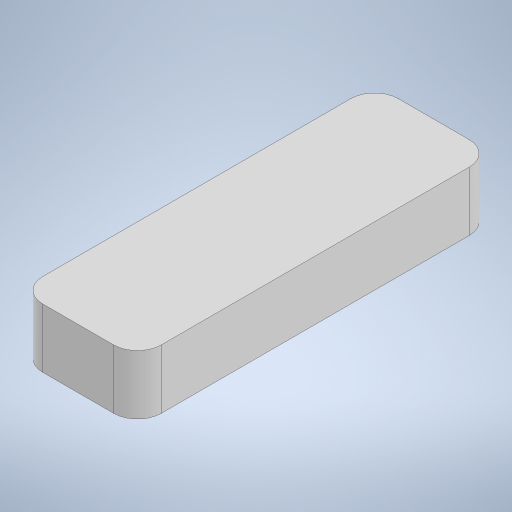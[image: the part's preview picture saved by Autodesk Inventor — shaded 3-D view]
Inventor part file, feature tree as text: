
AUTODESK INVENTOR PART (.ipt)
format: ipt  version: 2023 (Build 270158000, 158)  size: 203,264 bytes
history: native  units: mm
features: other x1, extrude x1, fillet x1, sketch x1
ambient origin geometry x8: Origin, YZ Plane, XZ Plane, XY Plane, X Axis, Y Axis, Z Axis, Center Point
bodies: Body1 (feature_tree)
feature tree (4):
  other  "Bryła1"
  extrude  "Wyciągnięcie proste1"  Depth=10.0mm
  fillet  "Zaokrąglenie1"  Radius=30.0mm
  sketch  "Szkic1"
